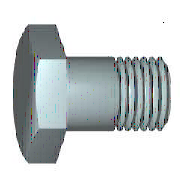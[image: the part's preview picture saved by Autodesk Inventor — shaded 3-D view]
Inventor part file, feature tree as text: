
AUTODESK INVENTOR PART (.ipt)
format: ipt  version: 2025.2 (Build 292293000, 293)  size: 196,608 bytes
history: native  units: mm (DEFAULTED — no unit token found)
features: chamfer x2, other x1, extrude x1, plane x1
ambient origin geometry x7: Origin, YZ Plane, XZ Plane, X Axis, Y Axis, Z Axis, Center Point
bodies: Solid1 (feature_tree)
feature tree (5):
  other  "Körper"
  extrude  "Kopf"  Depth=30.0mm
  chamfer  "Fase1"  Distance=26.0mm
  chamfer  "Fase2"  Distance=12.0mm
  plane  "Work Plane1"
